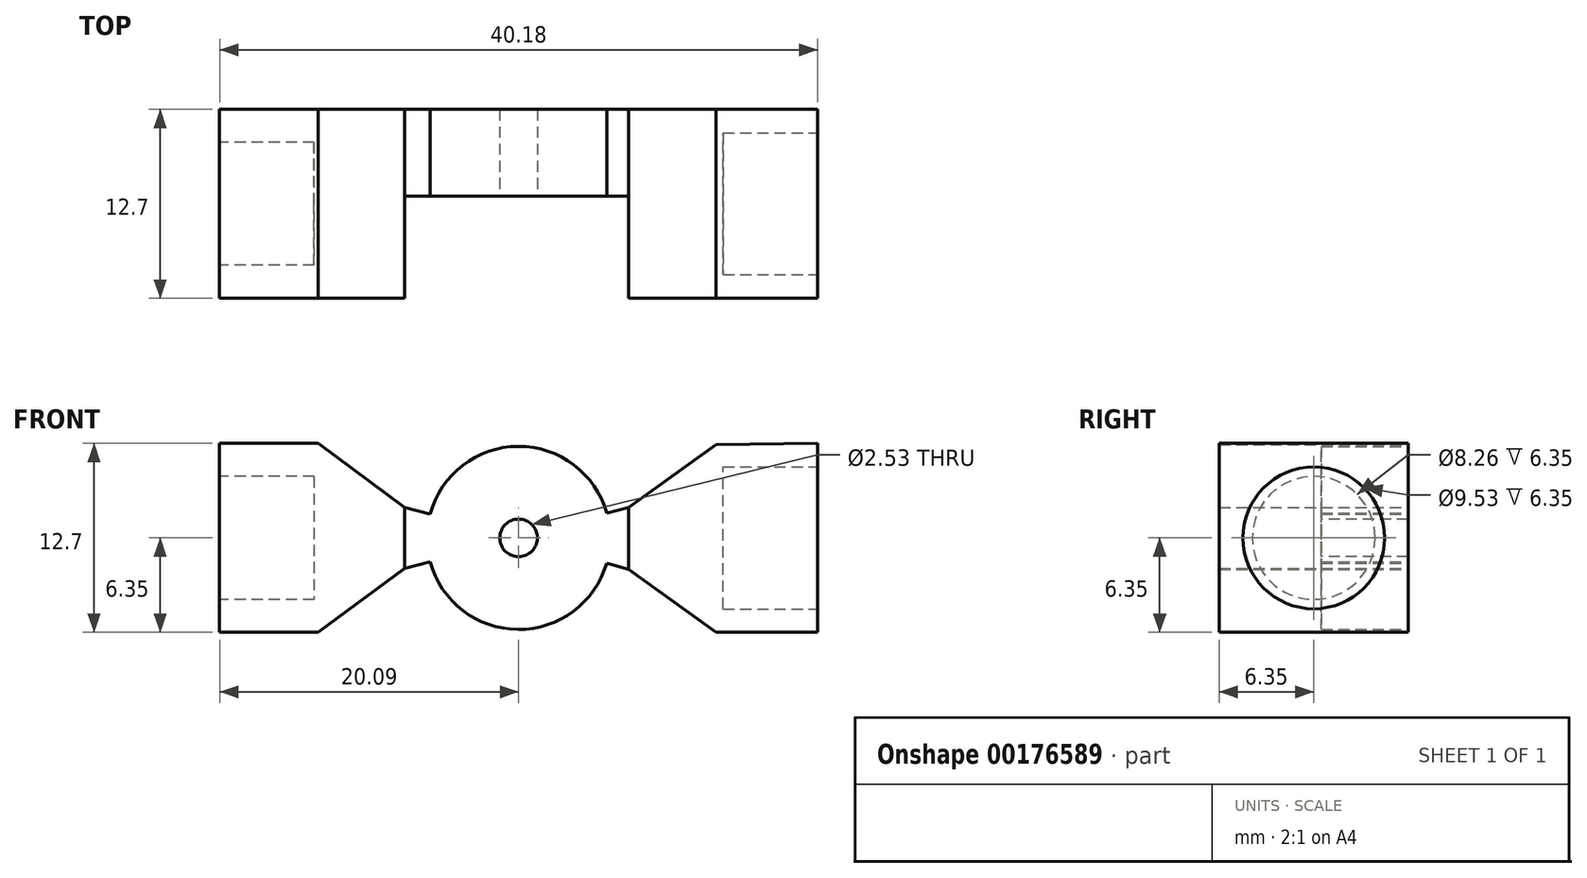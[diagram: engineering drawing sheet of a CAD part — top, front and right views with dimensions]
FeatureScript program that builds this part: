
annotation { "Feature Type Name" : "Feature", "Feature Type Description" : "" }
export const myFeature = defineFeature(function(context is Context, id is Id, definition is map)
    precondition{}
    {
        {
            var Q0;
            Q0=qCreatedBy(makeId("Front.planeOp"),FACE);
            var sketch = newSketch(context, id + "F0", { "sketchPlane" : qUnion([Q0])});
            skArc(sketch, "E0", {"start": v(5.93, 1.65) * mm, "mid": v(-0.03, 6.15) * mm, "end": v(-5.94, 1.6) * mm});
            skLineSegment(sketch, "E1", {"start": v(-20.1, 0) * mm, "end": v(-20.1, 6.35) * mm});
            skLineSegment(sketch, "E2", {"start": v(20.1, 0) * mm, "end": v(20.1, 6.35) * mm});
            skLineSegment(sketch, "E3", {"start": v(20.1, 0) * mm, "end": v(20.1, -6.35) * mm});
            skLineSegment(sketch, "E4", {"start": v(-20.1, 0) * mm, "end": v(-20.1, -6.35) * mm});
            skLineSegment(sketch, "E5", {"start": v(-20.1, 6.35) * mm, "end": v(-13.46, 6.35) * mm});
            skLineSegment(sketch, "E6", {"start": v(-13.46, 6.35) * mm, "end": v(-7.64, 2.06) * mm});
            skLineSegment(sketch, "E7", {"start": v(-7.64, 2.06) * mm, "end": v(-5.94, 1.6) * mm});
            skLineSegment(sketch, "E8", {"start": v(-20.1, -6.35) * mm, "end": v(-13.46, -6.35) * mm});
            skLineSegment(sketch, "E9", {"start": v(-13.46, -6.35) * mm, "end": v(-7.64, -2.06) * mm});
            skLineSegment(sketch, "E10", {"start": v(-7.64, -2.06) * mm, "end": v(-5.94, -1.6) * mm});
            skLineSegment(sketch, "E11", {"start": v(20.1, 6.35) * mm, "end": v(13.26, 6.28) * mm});
            skLineSegment(sketch, "E12", {"start": v(13.26, 6.28) * mm, "end": v(7.4, 2.06) * mm});
            skLineSegment(sketch, "E13", {"start": v(20.1, -6.35) * mm, "end": v(13.26, -6.35) * mm});
            skLineSegment(sketch, "E14", {"start": v(13.26, -6.35) * mm, "end": v(7.4, -2.13) * mm});
            skLineSegment(sketch, "E15", {"start": v(7.4, -2.13) * mm, "end": v(5.91, -1.7) * mm});
            skLineSegment(sketch, "E16", {"start": v(7.4, 2.06) * mm, "end": v(5.93, 1.65) * mm});
            skArc(sketch, "E17.trimOffspring", {"start": v(-5.94, -1.6) * mm, "mid": v(-0.05, -6.15) * mm, "end": v(5.91, -1.7) * mm});
            skLineSegment(sketch, "E18", {"start": v(-7.64, 2.06) * mm, "end": v(-7.64, -2.06) * mm});
            skLineSegment(sketch, "E19", {"start": v(7.4, 2.06) * mm, "end": v(7.4, -2.13) * mm});
            skSolve(sketch);
        }
        {
            var Q0;
            Q0=makeQuery(id+"F0.imprint","IMPRINT",FACE,{"disambiguationData":[TD([[makeQuery(id+"F0.imprint","IMPRINT",EDGE,{"derivedFrom":sQuery(id+"F0.wireOp",EDGE,"E1")}),-1.0]])]});
            var Q1;
            Q1=makeQuery(id+"F0.imprint","IMPRINT",FACE,{"disambiguationData":[TD([[makeQuery(id+"F0.imprint","IMPRINT",EDGE,{"derivedFrom":sQuery(id+"F0.wireOp",EDGE,"E0")}),1.0]])]});
            var Q2;
            Q2=makeQuery(id+"F0.imprint","IMPRINT",FACE,{"disambiguationData":[TD([[makeQuery(id+"F0.imprint","IMPRINT",EDGE,{"derivedFrom":sQuery(id+"F0.wireOp",EDGE,"E2")}),1.0]])]});
            extrude(context, id + "F1", {"entities" : qUnion([Q0, Q1, Q2]), "depth" : 12.7 * mm});
        }
        {
            var Q0;
            Q0=makeQuery(id+"F1.opExtrude","CAP_FACE",FACE,{"disambiguationData":[OSD([sQuery(id+"F0.wireOp",EDGE,"E0"),sQuery(id+"F0.wireOp",EDGE,"E1"),sQuery(id+"F0.wireOp",EDGE,"E2"),sQuery(id+"F0.wireOp",EDGE,"E3"),sQuery(id+"F0.wireOp",EDGE,"E4"),sQuery(id+"F0.wireOp",EDGE,"E5"),sQuery(id+"F0.wireOp",EDGE,"E6"),sQuery(id+"F0.wireOp",EDGE,"E7"),sQuery(id+"F0.wireOp",EDGE,"E8"),sQuery(id+"F0.wireOp",EDGE,"E9"),sQuery(id+"F0.wireOp",EDGE,"E10"),sQuery(id+"F0.wireOp",EDGE,"E11"),sQuery(id+"F0.wireOp",EDGE,"E12"),sQuery(id+"F0.wireOp",EDGE,"E13"),sQuery(id+"F0.wireOp",EDGE,"E14"),sQuery(id+"F0.wireOp",EDGE,"E15"),sQuery(id+"F0.wireOp",EDGE,"E16"),sQuery(id+"F0.wireOp",EDGE,"E17.trimOffspring")])],"isStart":false});
            var sketch = newSketch(context, id + "F2", { "sketchPlane" : qUnion([Q0])});
            skLineSegment(sketch, "E20", {"start": v(-7.64, 2.06) * mm, "end": v(-7.64, -2.06) * mm});
            skLineSegment(sketch, "E21", {"start": v(7.4, -2.13) * mm, "end": v(7.4, 2.06) * mm});
            skSolve(sketch);
        }
        {
            var Q0;
            Q0 = qSketchRegion(id + "F2", true);
            var Q1;
            Q1=makeQuery(id+"F2.imprint","IMPRINT",FACE,{"disambiguationData":[TD([[makeQuery(id+"F2.imprint","IMPRINT",EDGE,{"derivedFrom":sQuery(id+"F2.wireOp",EDGE,"E20")}),1.0]])]});
            extrude(context, id + "F3", {"entities" : qUnion([Q0, Q1]), "operationType" : NewBodyOperationType.REMOVE, "oppositeDirection" : true, "depth" : 6.86 * mm});
        }
        {
            var Q0;
            Q0=makeQuery(id+"F1.opExtrude","SWEPT_FACE",FACE,{"disambiguationData":[OSD([sQuery(id+"F0.wireOp",EDGE,"E1"),sQuery(id+"F0.wireOp",EDGE,"E4")])]});
            var sketch = newSketch(context, id + "F4", { "sketchPlane" : qUnion([Q0])});
            skCircle(sketch, "E22", {"center": v(6.35, 0) * mm, "radius": 4.13 * mm});
            skSolve(sketch);
        }
        {
            var Q0;
            Q0=makeQuery(id+"F4.imprint","IMPRINT",FACE,{"disambiguationData":[TD([[makeQuery(id+"F4.imprint","IMPRINT",EDGE,{"derivedFrom":sQuery(id+"F4.wireOp",EDGE,"E22")}),1.0]])]});
            extrude(context, id + "F5", {"entities" : qUnion([Q0]), "operationType" : NewBodyOperationType.REMOVE, "oppositeDirection" : true, "depth" : 6.35 * mm});
        }
        {
            var Q0;
            Q0=makeQuery(id+"F1.opExtrude","SWEPT_FACE",FACE,{"disambiguationData":[OSD([sQuery(id+"F0.wireOp",EDGE,"E2"),sQuery(id+"F0.wireOp",EDGE,"E3")])]});
            var sketch = newSketch(context, id + "F6", { "sketchPlane" : qUnion([Q0])});
            skCircle(sketch, "E23", {"center": v(-6.35, 0) * mm, "radius": 4.76 * mm});
            skSolve(sketch);
        }
        {
            var Q0;
            Q0 = qSketchRegion(id + "F6", true);
            extrude(context, id + "F7", {"entities" : qUnion([Q0]), "operationType" : NewBodyOperationType.REMOVE, "oppositeDirection" : true, "depth" : 6.35 * mm});
        }
        {
            var Q0;
            Q0=makeQuery(id+"F3.boolean.opBoolean","COPY",FACE,{"derivedFrom":makeQuery(id+"F3.opExtrude","CAP_FACE",FACE,{"disambiguationData":[OSD([sQuery(id+"F0.wireOp",EDGE,"E0"),sQuery(id+"F0.wireOp",EDGE,"E7"),sQuery(id+"F0.wireOp",EDGE,"E10"),sQuery(id+"F0.wireOp",EDGE,"E15"),sQuery(id+"F0.wireOp",EDGE,"E16"),sQuery(id+"F0.wireOp",EDGE,"E17.trimOffspring"),sQuery(id+"F2.wireOp",EDGE,"E20"),sQuery(id+"F2.wireOp",EDGE,"E21")])],"isStart":false})});
            var sketch = newSketch(context, id + "F8", { "sketchPlane" : qUnion([Q0])});
            skCircle(sketch, "E24", {"center": v(0, 0) * mm, "radius": 1.26 * mm});
            skSolve(sketch);
        }
        {
            var Q0;
            Q0 = qSketchRegion(id + "F8", true);
            extrude(context, id + "F9", {"entities" : qUnion([Q0]), "operationType" : NewBodyOperationType.REMOVE, "oppositeDirection" : true, "depth" : 25.4 * mm});
        }
    });
